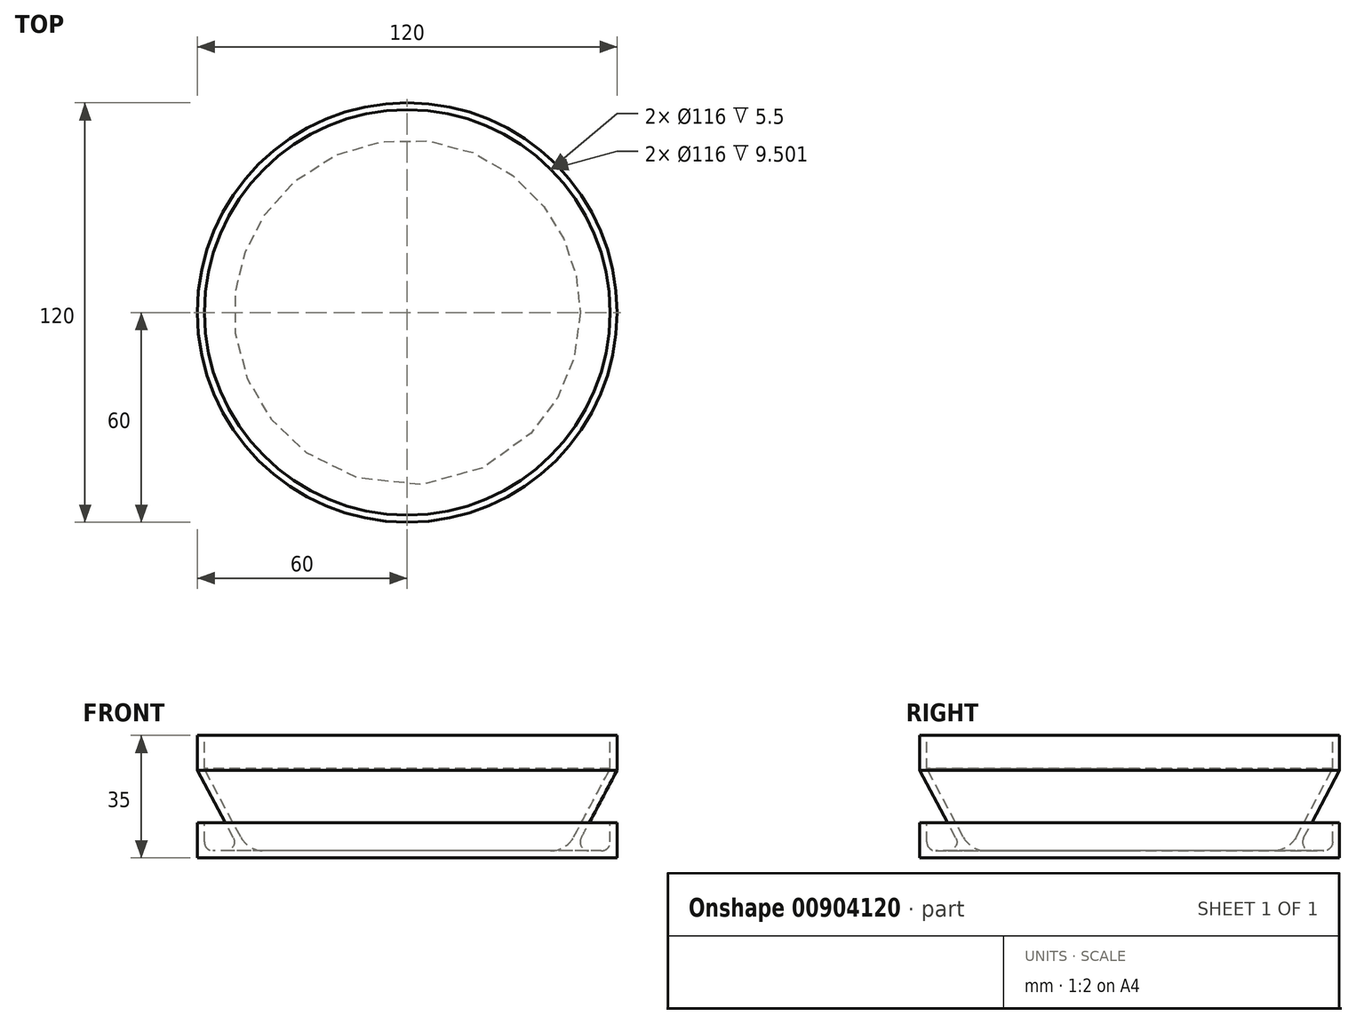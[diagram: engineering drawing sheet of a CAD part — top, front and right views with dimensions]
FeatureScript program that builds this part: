
annotation { "Feature Type Name" : "Feature", "Feature Type Description" : "" }
export const myFeature = defineFeature(function(context is Context, id is Id, definition is map)
    precondition{}
    {
        {
            var Q0;
            Q0=qCreatedBy(makeId("Front.planeOp"),FACE);
            var sketch = newSketch(context, id + "F0", { "sketchPlane" : qUnion([Q0])});
            skLineSegment(sketch, "E0", {"start": v(0, 0) * mm, "end": v(-46.7, 0) * mm});
            skLineSegment(sketch, "E1", {"start": v(-49.72, 5.67) * mm, "end": v(-60, 25) * mm});
            skLineSegment(sketch, "E2", {"start": v(-60, 25) * mm, "end": v(-60, 35) * mm});
            skLineSegment(sketch, "E3", {"start": v(-60, 35) * mm, "end": v(-58, 35) * mm});
            skLineSegment(sketch, "E4", {"start": v(-58, 35) * mm, "end": v(-58, 25.5) * mm});
            skLineSegment(sketch, "E5.0", {"start": v(-47.62, 5.98) * mm, "end": v(-58, 25.5) * mm});
            skLineSegment(sketch, "E6.0", {"start": v(0, 2) * mm, "end": v(-41, 2) * mm});
            skLineSegment(sketch, "E7", {"start": v(-46.7, 0) * mm, "end": v(-60, 0) * mm});
            skLineSegment(sketch, "E8", {"start": v(-60, 0) * mm, "end": v(-60, 10) * mm});
            skLineSegment(sketch, "E9", {"start": v(-60, 10) * mm, "end": v(-58, 10) * mm});
            skLineSegment(sketch, "E10", {"start": v(-58, 10) * mm, "end": v(-58, 4.5) * mm});
            skLineSegment(sketch, "E11", {"start": v(-55.5, 2) * mm, "end": v(-51.93, 2) * mm});
            skLineSegment(sketch, "E12", {"start": v(0, 2) * mm, "end": v(0, 0) * mm});
            skPoint(sketch, "E13.visualSharp", {"position": v(-47.77, 2) * mm});
            skArc(sketch, "E13.filletArc", {"start": v(-51.93, 2) * mm, "mid": v(-49.79, 3.21) * mm, "end": v(-49.72, 5.67) * mm});
            skPoint(sketch, "E14.visualSharp", {"position": v(-45.5, 2) * mm});
            skArc(sketch, "E14.filletArc", {"start": v(-47.62, 5.98) * mm, "mid": v(-44.86, 3.07) * mm, "end": v(-41, 2) * mm});
            skPoint(sketch, "E15.visualSharp", {"position": v(-58, 2) * mm});
            skArc(sketch, "E15.filletArc", {"start": v(-58, 4.5) * mm, "mid": v(-57.27, 2.73) * mm, "end": v(-55.5, 2) * mm});
            skSolve(sketch);
        }
        {
            var Q0;
            Q0=makeQuery(id+"F0.imprint","IMPRINT",FACE,{"disambiguationData":[TD([[makeQuery(id+"F0.imprint","IMPRINT",EDGE,{"derivedFrom":sQuery(id+"F0.wireOp",EDGE,"E0")}),-1.0]])]});
            var Q1;
            Q1=sQuery(id+"F0.wireOp",EDGE,"E12");
            revolve(context, id + "F1", {"surfaceOperationType" : NewSurfaceOperationType.NEW, "entities" : qUnion([Q0]), "axis" : qUnion([Q1]), "revolveType" : RevolveType.FULL});
        }
    });
